# Revit family: toilet seats-hansgrohe-60197XXX-EluPura S WC seat and cover with top fix, SoftClose and QuickRelease
name_source: partatom
category: Sanitärinstallationen
units: mm (PartAtom-declared; Revit-internal decimal feet)

## family parameters
Arbeitsebenenbasiert = Nein
Beim Laden mit Abzugskörper schneiden = Nein
Bemaßung runder Anschluss = Durchmesser verwenden
Beschriftungsausrichtung beibehalten = Nein
Gemeinsam genutzt = Ja
Immer vertikal = Ja
OmniClass-Nummer = 23.45.00.00
OmniClass-Titel = Sanitary, Laundry, and Cleaning Equipment
Raumberechnungspunkt = Nein
Teiletyp = Normal

## types (2) — shared parameters
60196-60196450-GLOSSY_WHITE-200_RX0RY0RZ0TX0TY0TZ0_V = Nein
60196-60196450-GLOSSY_WHITE-400_RX0RY0RZ0TX0TY0TZ0_V = Nein
ARTNR = 60197450
BASENUMBER = 60197
BIMOBJECT = Sanitary: Toilet Seats
CATALOG = Hansgrohe
COLLECTION = toilet seats
COLLECTIONSET = EluPura S
DEPTH = 440
DESIGN = Germany
GTINCODE = 4059625470114
Hersteller = Hansgrohe
IDNR = 2
IFC = Furnishing element
NAME = EluPura S WC seat and cover with top fix, SoftClose and QuickRelease
NBSYN = $BASENUMBER.-$ARTNR.-$SURFACE.-$LODLEVEL.
NN = EluPura S WC seat and cover with top fix
OBJECTTYPE = Object (single object)
OMNICLASS = 23-31 19 00 | Toilets
PERMALINK = 60197XXX
PRODUCTURL = https://pro.hansgrohe.com
REGION = Worldwide
SPECIFICATION = Surfaces:  - 60197450 White   Specification:  • consists of: WC seat, cover  • material: Urea  • degree of gloss: glossy  • with comfortable SoftClose mechanism • QuickRelease: quick removable toilet seat and cover
SURFACE = GLOSSY_WHITE
UNICLASS2015 = Pr_40_20_93_95 | WC seats and covers
UNICLASS_2015_CODE = 40_20_93_95
WEIGHT = 4.8
WIDTH = 366
zero-valued in all types: HEIGHT, Vorgabe-Ansicht

## per-type parameters (varying)
| type | 60197-60197450-GLOSSY_WHITE-200_RX0RY0RZ0TX0TY0TZ0_V | 60197-60197450-GLOSSY_WHITE-400_RX0RY0RZ0TX0TY0TZ0_V | LODLEVEL |
| 60197-60197450-GLOSSY_WHITE-200 | Ja | Nein | 200 |
| 60197-60197450-GLOSSY_WHITE-400 | Nein | Ja | 400 |

note: column(s) folded — value = type name in every type: LINA, Modell, NB

## geometry (parser evidence)
native form markers: Sweep x20
no freeform markers — native parametric forms only
